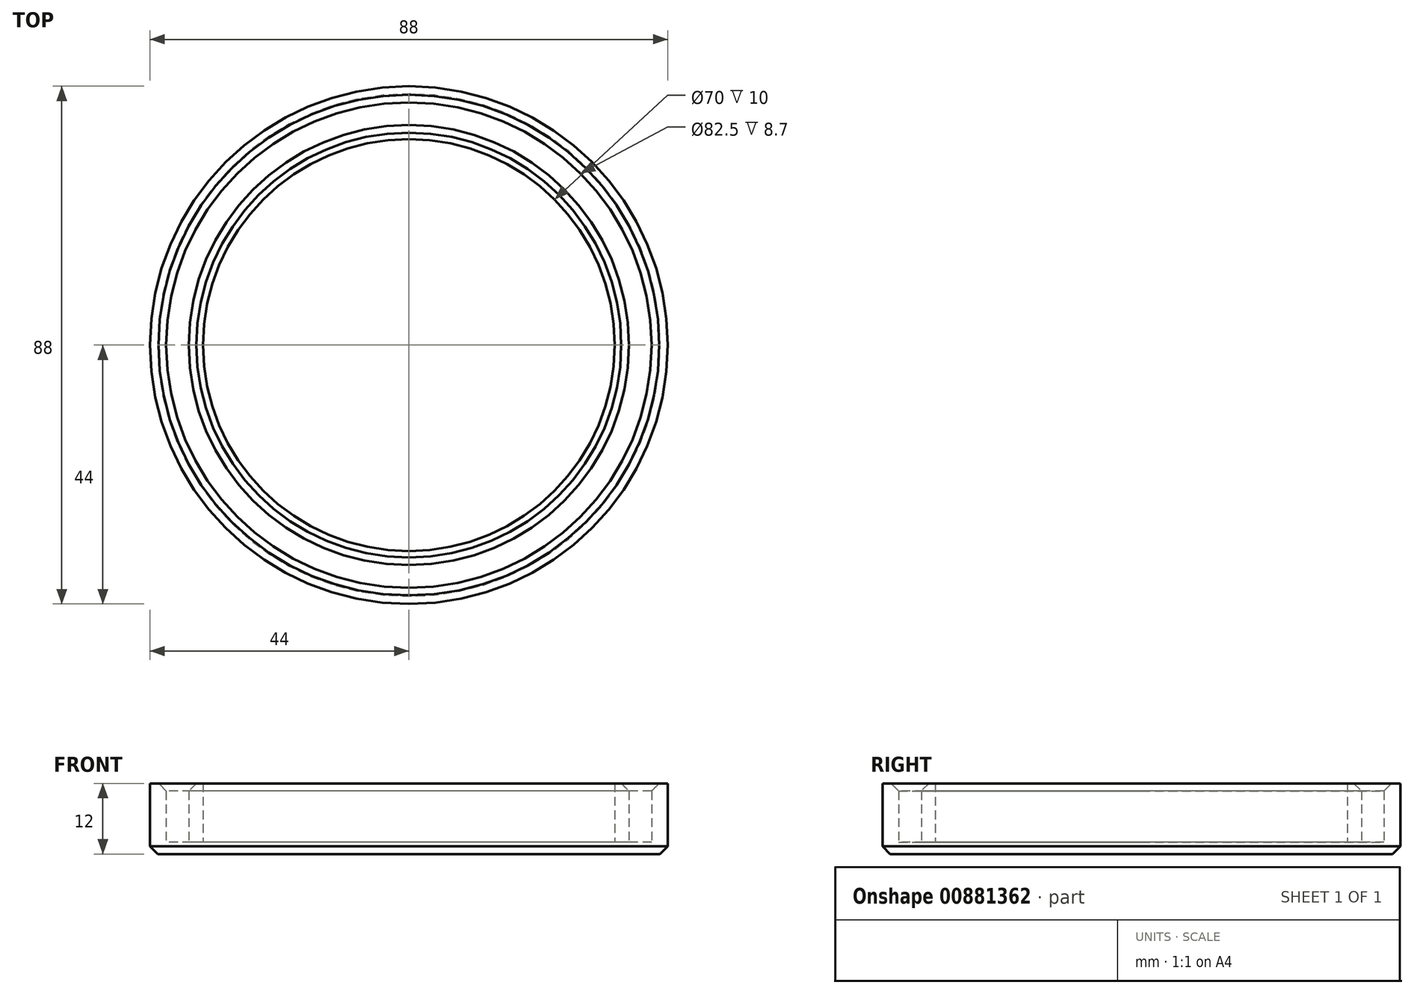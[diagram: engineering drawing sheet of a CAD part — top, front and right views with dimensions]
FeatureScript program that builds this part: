
annotation { "Feature Type Name" : "Feature", "Feature Type Description" : "" }
export const myFeature = defineFeature(function(context is Context, id is Id, definition is map)
    precondition{}
    {
        {
            var Q0;
            Q0=qCreatedBy(makeId("Top.planeOp"),FACE);
            var sketch = newSketch(context, id + "F0", { "sketchPlane" : qUnion([Q0])});
            skCircle(sketch, "E0", {"center": v(0, 0) * mm, "radius": 44 * mm});
            skSolve(sketch);
        }
        {
            var Q0;
            Q0=makeQuery(id+"F0.imprint","IMPRINT",FACE,{"disambiguationData":[TD([[makeQuery(id+"F0.imprint","IMPRINT",EDGE,{"derivedFrom":sQuery(id+"F0.wireOp",EDGE,"E0")}),1.0]])]});
            extrude(context, id + "F1", {"entities" : qUnion([Q0]), "depth" : 2 * mm, "offsetDistance" : 25 * mm});
        }
        {
            var Q0;
            Q0=makeQuery(id+"F1.opExtrude","CAP_FACE",FACE,{"disambiguationData":[OSD([sQuery(id+"F0.wireOp",EDGE,"E0")])],"isStart":false});
            var sketch = newSketch(context, id + "F2", { "sketchPlane" : qUnion([Q0])});
            skCircle(sketch, "E1", {"center": v(0, 0) * mm, "radius": 37.4 * mm});
            skCircle(sketch, "E2", {"center": v(0, 0) * mm, "radius": 41.25 * mm});
            skCircle(sketch, "E3", {"center": v(0, 0) * mm, "radius": 35 * mm});
            skSolve(sketch);
        }
        {
            var Q0;
            Q0=makeQuery(id+"F2.imprint","IMPRINT",FACE,{"disambiguationData":[TD([[makeQuery(id+"F2.imprint","IMPRINT",EDGE,{"derivedFrom":sQuery(id+"F2.wireOp",EDGE,"E2")}),-1.0]])]});
            var Q1;
            Q1=makeQuery(id+"F2.imprint","IMPRINT",FACE,{"disambiguationData":[TD([[makeQuery(id+"F2.imprint","IMPRINT",EDGE,{"derivedFrom":sQuery(id+"F2.wireOp",EDGE,"E1")}),1.0]])]});
            extrude(context, id + "F3", {"entities" : qUnion([Q0, Q1]), "operationType" : NewBodyOperationType.ADD, "depth" : 10 * mm, "offsetDistance" : 25 * mm});
        }
        {
            var Q0;
            Q0=makeQuery(id+"F3.opExtrude","CAP_EDGE",EDGE,{"disambiguationData":[OSD([sQuery(id+"F2.wireOp",EDGE,"E2")])],"isStart":false});
            var Q1;
            Q1=makeQuery(id+"F3.opExtrude","CAP_EDGE",EDGE,{"disambiguationData":[OSD([sQuery(id+"F2.wireOp",EDGE,"E1")])],"isStart":false});
            var Q2;
            Q2=makeQuery(id+"F1.opExtrude","CAP_EDGE",EDGE,{"disambiguationData":[OSD([sQuery(id+"F0.wireOp",EDGE,"E0")])],"isStart":true});
            chamfer(context, id + "F4", {"entities" : qUnion([Q0, Q1, Q2]), "width" : 1.3 * mm, "tangentPropagation" : true});
        }
    });
